# Revit family: KEUCO_14916010000_
name_source: partatom
category: Generic Models
revit_build: Autodesk Revit 2016 (Build: 20150220_1215(x64)
units: mm (PartAtom-declared; Revit-internal decimal feet)

## family parameters
Always vertical = No
Can host rebar = No
Cut with Voids When Loaded = No
Part Type = Normal
Room Calculation Point = No
Round Connector Dimension = Use Diameter
Shared = No
Work Plane-Based = Yes

## types (3) — shared parameters
Default Elevation = 1219 mm
Description = --
Manufacturer = KEUCO
Serie = Plan
Stange Breite = 38 mm  [stored 0.124672 ft]
URL = https://www.keuco.com
Verwendung = BI / DU / GWC / WA / WP
zero-valued in all types: Gewicht

## per-type parameters (varying)
| type | Ausschreibungstext | Material |
| 14916010000 | KEUCO PLAN Handtuchhaken 14916010000
Hochglanzverchromter Handtuchhaken 
in ästhetischem, funktionalem Design
zylindrische Grundform, abgerundete Kanten, leicht zu reinigen
Ausladung 38 mm , Zylinderdurchmesser 15 mm, Kopfdurchmesser 21 mm
Der Handtuchhaken wird verdeckt angebracht
Lieferung inkl. korrosionsfreiem Befestigungsmaterial | Verchromt |
| 14916070000 | KEUCO PLAN Handtuchhaken 14916070000
Zeitloser Handtuchhaken 
aus hochwertigem Edelstahl 
in ästhetischem, funktionalem Design
zylindrische Grundform, abgerundete Kanten, leicht zu reinigen
Ausladung 38 mm, Zylinderdurchmesser 15 mm, Kopfdurchmesser 21 mm
Der Handtuchhaken wird verdeckt angebracht
Lieferung inkl. korrosionsfreiem Befestigungsmaterial | Edelstahl |
| 14916170000 | KEUCO PLAN Handtuchhaken 14916170000
Handtuchhaken aus silber-eloxiertem Aluminium (E6 EV1) 
in ästhetischem, funktionalem Design
zylindrische Grundform, abgerundete Kanten, leicht zu reinigen
Ausladung 38 mm, Zylinderdurchmesser 15 mm, Kopfdurchmesser 21 mm
Der Handtuchhaken wird verdeckt angebracht
Lieferung inkl. korrosionsfreiem Befestigungsmaterial | Aluminium silber-eloxiert (E6 EV1) |

note: column(s) folded — value = type name in every type: Artikelnummer

note: [stored X ft] marks values corroborated as IEEE doubles in the binary element streams (Revit-internal decimal feet)

## geometry (parser evidence)
native form markers: Sweep x3
no freeform markers — native parametric forms only
